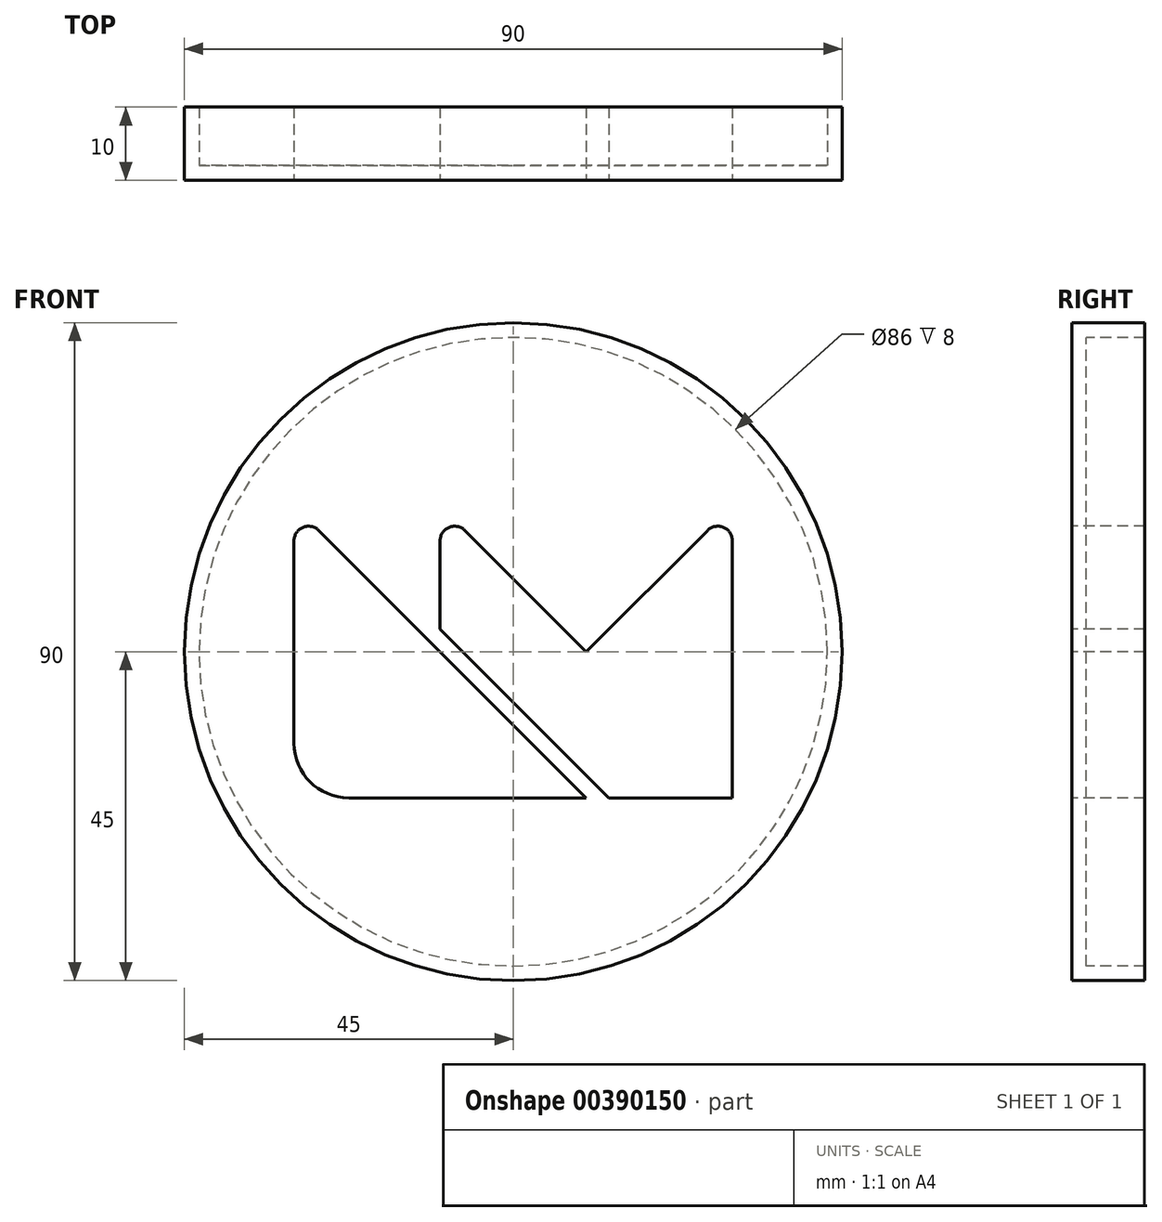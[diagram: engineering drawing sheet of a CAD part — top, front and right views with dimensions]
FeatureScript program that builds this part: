
annotation { "Feature Type Name" : "Feature", "Feature Type Description" : "" }
export const myFeature = defineFeature(function(context is Context, id is Id, definition is map)
    precondition{}
    {
        {
            var Q0;
            Q0=qCreatedBy(makeId("Front.planeOp"),FACE);
            var sketch = newSketch(context, id + "F0", { "sketchPlane" : qUnion([Q0])});
            skLineSegment(sketch, "E0.bottom", {"start": v(7.5, 0) * mm, "end": v(20, 0) * mm});
            skLineSegment(sketch, "E0.left", {"start": v(0, 7.5) * mm, "end": v(0, 20) * mm});
            skPoint(sketch, "E1.visualSharp", {"position": v(0, 0) * mm});
            skArc(sketch, "E1.filletArc", {"start": v(0, 7.5) * mm, "mid": v(2.2, 2.2) * mm, "end": v(7.5, 0) * mm});
            skLineSegment(sketch, "E2.bottom", {"start": v(20, 0) * mm, "end": v(40, 0) * mm});
            skLineSegment(sketch, "E3.right", {"start": v(0, 20) * mm, "end": v(0, 35.17) * mm});
            skLineSegment(sketch, "E4.left", {"start": v(20, 23.07) * mm, "end": v(20, 35.17) * mm});
            skLineSegment(sketch, "E5", {"start": v(23.41, 36.59) * mm, "end": v(40, 20) * mm});
            skLineSegment(sketch, "E6", {"start": v(40, 20) * mm, "end": v(56.59, 36.59) * mm});
            skLineSegment(sketch, "E7", {"start": v(3.41, 36.59) * mm, "end": v(20, 20) * mm});
            skLineSegment(sketch, "E8", {"start": v(43.07, 0) * mm, "end": v(60, 0) * mm});
            skLineSegment(sketch, "E9", {"start": v(60, 35.17) * mm, "end": v(60, 0) * mm});
            skPoint(sketch, "E10.visualSharp", {"position": v(0, 40) * mm});
            skArc(sketch, "E10.filletArc", {"start": v(3.41, 36.59) * mm, "mid": v(1.23, 37.02) * mm, "end": v(0, 35.17) * mm});
            skPoint(sketch, "E11.visualSharp", {"position": v(60, 40) * mm});
            skArc(sketch, "E11.filletArc", {"start": v(60, 35.17) * mm, "mid": v(58.77, 37.02) * mm, "end": v(56.59, 36.59) * mm});
            skPoint(sketch, "E12.visualSharp", {"position": v(20, 40) * mm});
            skArc(sketch, "E12.filletArc", {"start": v(23.41, 36.59) * mm, "mid": v(21.23, 37.02) * mm, "end": v(20, 35.17) * mm});
            skLineSegment(sketch, "E13", {"start": v(20, 20) * mm, "end": v(40, 0) * mm});
            skLineSegment(sketch, "E14", {"start": v(43.07, 0) * mm, "end": v(20, 23.07) * mm});
            skSolve(sketch);
        }
        {
            var Q0;
            Q0=makeQuery(id+"F0.imprint","IMPRINT",FACE,{"disambiguationData":[TD([[makeQuery(id+"F0.imprint","IMPRINT",EDGE,{"derivedFrom":sQuery(id+"F0.wireOp",EDGE,"E0.bottom")}),1.0]])]});
            var Q1;
            Q1=makeQuery(id+"F0.imprint","IMPRINT",FACE,{"disambiguationData":[TD([[makeQuery(id+"F0.imprint","IMPRINT",EDGE,{"derivedFrom":sQuery(id+"F0.wireOp",EDGE,"E5")}),-1.0]])]});
            extrude(context, id + "F1", {"entities" : qUnion([Q0, Q1]), "oppositeDirection" : true, "depth" : 10 * mm});
        }
        {
            var Q0;
            Q0=makeQuery(id+"F1.opExtrude","CAP_FACE",FACE,{"disambiguationData":[OSD([sQuery(id+"F0.wireOp",EDGE,"E0.bottom"),sQuery(id+"F0.wireOp",EDGE,"E0.left"),sQuery(id+"F0.wireOp",EDGE,"E1.filletArc"),sQuery(id+"F0.wireOp",EDGE,"E2.bottom"),sQuery(id+"F0.wireOp",EDGE,"E3.right"),sQuery(id+"F0.wireOp",EDGE,"E7"),sQuery(id+"F0.wireOp",EDGE,"E10.filletArc"),sQuery(id+"F0.wireOp",EDGE,"E13")])],"isStart":true});
            var sketch = newSketch(context, id + "F2", { "sketchPlane" : qUnion([Q0])});
            skCircle(sketch, "E15", {"center": v(30, 20) * mm, "radius": 45 * mm});
            skSolve(sketch);
        }
        {
            var Q0;
            Q0 = qSketchRegion(id + "F2", true);
            var Q1;
            Q1=makeQuery(id+"F1.opExtrude","CAP_FACE",FACE,{"disambiguationData":[OSD([sQuery(id+"F0.wireOp",EDGE,"E0.bottom"),sQuery(id+"F0.wireOp",EDGE,"E0.left"),sQuery(id+"F0.wireOp",EDGE,"E1.filletArc"),sQuery(id+"F0.wireOp",EDGE,"E2.bottom"),sQuery(id+"F0.wireOp",EDGE,"E3.right"),sQuery(id+"F0.wireOp",EDGE,"E7"),sQuery(id+"F0.wireOp",EDGE,"E10.filletArc"),sQuery(id+"F0.wireOp",EDGE,"E13")])],"isStart":false});
            extrude(context, id + "F3", {"entities" : qUnion([Q0]), "endBound" : BoundingType.UP_TO_SURFACE, "oppositeDirection" : true, "endBoundEntityFace" : qUnion([Q1]), "depth" : 25 * mm});
        }
        {
            var Q0;
            Q0=makeQuery(id+"F3.opExtrude","CAP_FACE",FACE,{"disambiguationData":[OSD([sQuery(id+"F2.wireOp",EDGE,"E15")])],"isStart":false});
            shell(context, id + "F4", {"entities" : qUnion([Q0]), "thickness" : 2 * mm});
        }
    });
